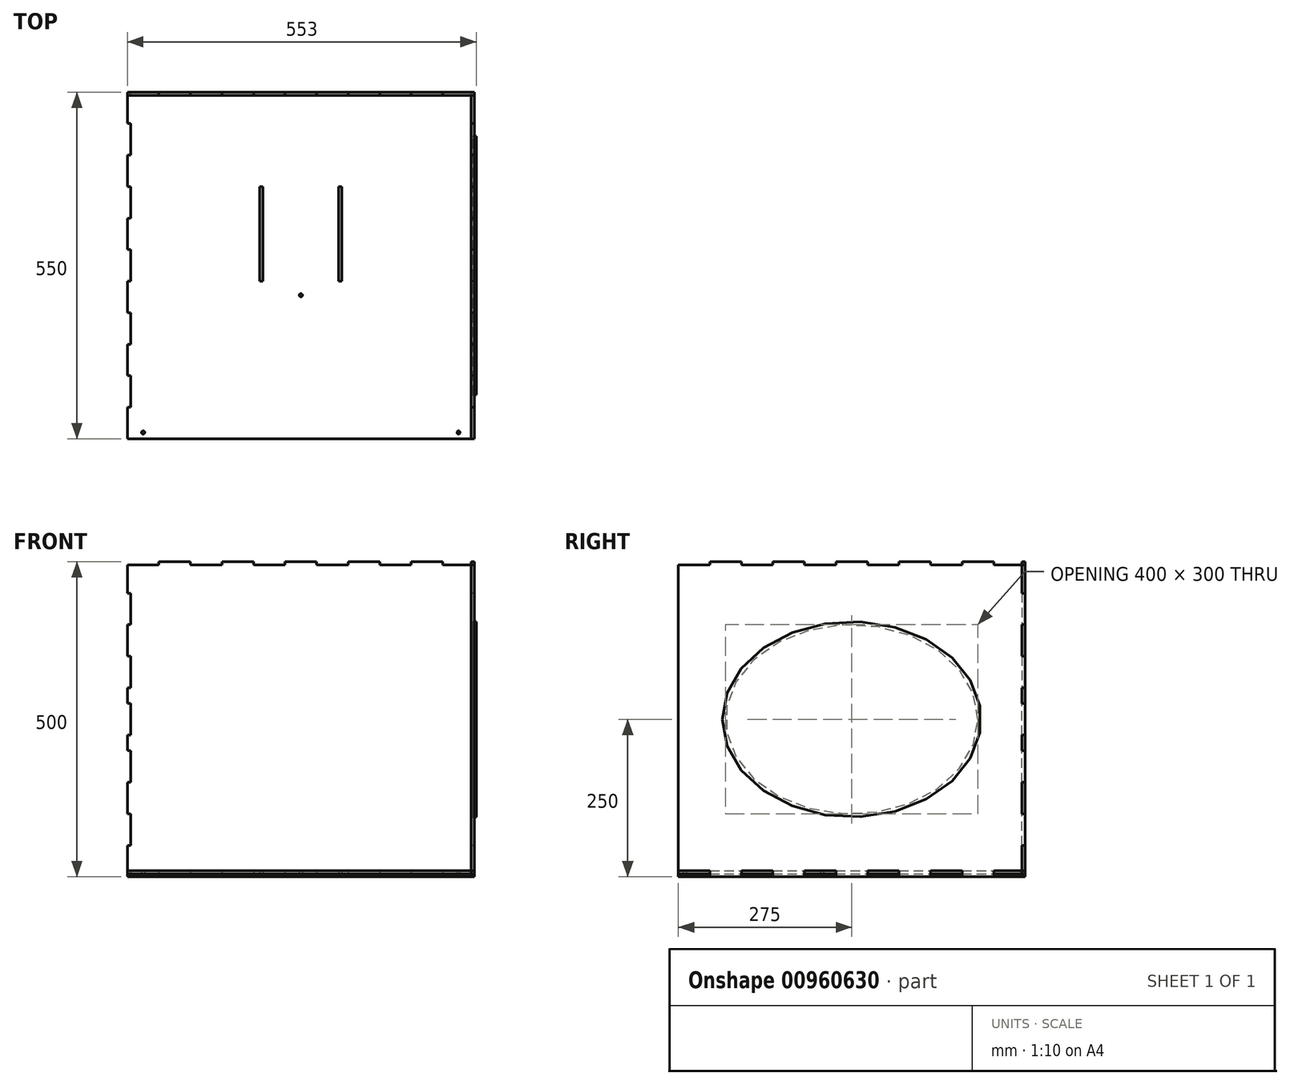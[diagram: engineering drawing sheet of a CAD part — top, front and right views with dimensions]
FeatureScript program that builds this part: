
annotation { "Feature Type Name" : "Feature", "Feature Type Description" : "" }
export const myFeature = defineFeature(function(context is Context, id is Id, definition is map)
    precondition{}
    {
        {
            var Q0;
            Q0=qCreatedBy(makeId("Top.planeOp"),FACE);
            var sketch = newSketch(context, id + "F0", { "sketchPlane" : qUnion([Q0])});
            skPoint(sketch, "E0.middle", {"position": v(0, 0) * mm});
            skLineSegment(sketch, "E1", {"start": v(275, -275) * mm, "end": v(275, -225) * mm});
            skLineSegment(sketch, "E2", {"start": v(275, -225) * mm, "end": v(270, -225) * mm});
            skLineSegment(sketch, "E3", {"start": v(270, -225) * mm, "end": v(270, -175) * mm});
            skLineSegment(sketch, "E4", {"start": v(270, -175) * mm, "end": v(275, -175) * mm});
            skLineSegment(sketch, "E5.0.1.0", {"start": v(270, -125) * mm, "end": v(270, -75) * mm});
            skLineSegment(sketch, "E5.0.1.1", {"start": v(270, -75) * mm, "end": v(275, -75) * mm});
            skLineSegment(sketch, "E5.0.1.2", {"start": v(275, -175) * mm, "end": v(275, -125) * mm});
            skLineSegment(sketch, "E5.0.1.3", {"start": v(275, -125) * mm, "end": v(270, -125) * mm});
            skLineSegment(sketch, "E5.0.2.0", {"start": v(270, -25) * mm, "end": v(270, 25) * mm});
            skLineSegment(sketch, "E5.0.2.1", {"start": v(270, 25) * mm, "end": v(275, 25) * mm});
            skLineSegment(sketch, "E5.0.2.2", {"start": v(275, -75) * mm, "end": v(275, -25) * mm});
            skLineSegment(sketch, "E5.0.2.3", {"start": v(275, -25) * mm, "end": v(270, -25) * mm});
            skLineSegment(sketch, "E5.0.3.0", {"start": v(270, 75) * mm, "end": v(270, 125) * mm});
            skLineSegment(sketch, "E5.0.3.1", {"start": v(270, 125) * mm, "end": v(275, 125) * mm});
            skLineSegment(sketch, "E5.0.3.2", {"start": v(275, 25) * mm, "end": v(275, 75) * mm});
            skLineSegment(sketch, "E5.0.3.3", {"start": v(275, 75) * mm, "end": v(270, 75) * mm});
            skLineSegment(sketch, "E5.0.4.0", {"start": v(270, 175) * mm, "end": v(270, 225) * mm});
            skLineSegment(sketch, "E5.0.4.1", {"start": v(270, 225) * mm, "end": v(275, 225) * mm});
            skLineSegment(sketch, "E5.0.4.2", {"start": v(275, 125) * mm, "end": v(275, 175) * mm});
            skLineSegment(sketch, "E5.0.4.3", {"start": v(275, 175) * mm, "end": v(270, 175) * mm});
            skLineSegment(sketch, "E5.direction1", {"start": v(275, -275) * mm, "end": v(300, -275) * mm, "construction": true});
            skLineSegment(sketch, "E5.direction2", {"start": v(275, -275) * mm, "end": v(275, -175) * mm, "construction": true});
            skLineSegment(sketch, "E6", {"start": v(-275, -275) * mm, "end": v(-275, -225) * mm});
            skLineSegment(sketch, "E7", {"start": v(-275, -225) * mm, "end": v(-270, -225) * mm});
            skLineSegment(sketch, "E8", {"start": v(-270, -225) * mm, "end": v(-270, -175) * mm});
            skLineSegment(sketch, "E9", {"start": v(-270, -175) * mm, "end": v(-275, -175) * mm});
            skLineSegment(sketch, "E10.0.1.0", {"start": v(-270, -125) * mm, "end": v(-270, -75) * mm});
            skLineSegment(sketch, "E10.0.1.1", {"start": v(-275, -175) * mm, "end": v(-275, -125) * mm});
            skLineSegment(sketch, "E10.0.1.2", {"start": v(-270, -75) * mm, "end": v(-275, -75) * mm});
            skLineSegment(sketch, "E10.0.1.3", {"start": v(-275, -125) * mm, "end": v(-270, -125) * mm});
            skLineSegment(sketch, "E10.0.2.0", {"start": v(-270, -25) * mm, "end": v(-270, 25) * mm});
            skLineSegment(sketch, "E10.0.2.1", {"start": v(-275, -75) * mm, "end": v(-275, -25) * mm});
            skLineSegment(sketch, "E10.0.2.2", {"start": v(-270, 25) * mm, "end": v(-275, 25) * mm});
            skLineSegment(sketch, "E10.0.2.3", {"start": v(-275, -25) * mm, "end": v(-270, -25) * mm});
            skLineSegment(sketch, "E10.0.3.0", {"start": v(-270, 75) * mm, "end": v(-270, 125) * mm});
            skLineSegment(sketch, "E10.0.3.1", {"start": v(-275, 25) * mm, "end": v(-275, 75) * mm});
            skLineSegment(sketch, "E10.0.3.2", {"start": v(-270, 125) * mm, "end": v(-275, 125) * mm});
            skLineSegment(sketch, "E10.0.3.3", {"start": v(-275, 75) * mm, "end": v(-270, 75) * mm});
            skLineSegment(sketch, "E10.0.4.0", {"start": v(-270, 175) * mm, "end": v(-270, 225) * mm});
            skLineSegment(sketch, "E10.0.4.1", {"start": v(-275, 125) * mm, "end": v(-275, 175) * mm});
            skLineSegment(sketch, "E10.0.4.2", {"start": v(-270, 225) * mm, "end": v(-275, 225) * mm});
            skLineSegment(sketch, "E10.0.4.3", {"start": v(-275, 175) * mm, "end": v(-270, 175) * mm});
            skLineSegment(sketch, "E10.direction1", {"start": v(-275, -275) * mm, "end": v(-250, -275) * mm, "construction": true});
            skLineSegment(sketch, "E10.direction2", {"start": v(-275, -275) * mm, "end": v(-275, -175) * mm, "construction": true});
            skLineSegment(sketch, "E11", {"start": v(-275, -275) * mm, "end": v(275, -275) * mm});
            skLineSegment(sketch, "E12", {"start": v(275, 225) * mm, "end": v(275, 275) * mm});
            skLineSegment(sketch, "E13", {"start": v(-275, 225) * mm, "end": v(-275, 275) * mm});
            skLineSegment(sketch, "E14", {"start": v(-275, 275) * mm, "end": v(-225, 275) * mm});
            skLineSegment(sketch, "E15", {"start": v(-225, 275) * mm, "end": v(-225, 270) * mm});
            skLineSegment(sketch, "E16", {"start": v(-225, 270) * mm, "end": v(-175, 270) * mm});
            skLineSegment(sketch, "E17", {"start": v(-175, 270) * mm, "end": v(-175, 275) * mm});
            skLineSegment(sketch, "E18.1.0.0", {"start": v(-175, 275) * mm, "end": v(-125, 275) * mm});
            skLineSegment(sketch, "E18.1.0.1", {"start": v(-125, 270) * mm, "end": v(-75, 270) * mm});
            skLineSegment(sketch, "E18.1.0.2", {"start": v(-75, 270) * mm, "end": v(-75, 275) * mm});
            skLineSegment(sketch, "E18.1.0.3", {"start": v(-125, 275) * mm, "end": v(-125, 270) * mm});
            skLineSegment(sketch, "E18.2.0.0", {"start": v(-75, 275) * mm, "end": v(-25, 275) * mm});
            skLineSegment(sketch, "E18.2.0.1", {"start": v(-25, 270) * mm, "end": v(25, 270) * mm});
            skLineSegment(sketch, "E18.2.0.2", {"start": v(25, 270) * mm, "end": v(25, 275) * mm});
            skLineSegment(sketch, "E18.2.0.3", {"start": v(-25, 275) * mm, "end": v(-25, 270) * mm});
            skLineSegment(sketch, "E18.3.0.0", {"start": v(25, 275) * mm, "end": v(75, 275) * mm});
            skLineSegment(sketch, "E18.3.0.1", {"start": v(75, 270) * mm, "end": v(125, 270) * mm});
            skLineSegment(sketch, "E18.3.0.2", {"start": v(125, 270) * mm, "end": v(125, 275) * mm});
            skLineSegment(sketch, "E18.3.0.3", {"start": v(75, 275) * mm, "end": v(75, 270) * mm});
            skLineSegment(sketch, "E18.4.0.0", {"start": v(125, 275) * mm, "end": v(175, 275) * mm});
            skLineSegment(sketch, "E18.4.0.1", {"start": v(175, 270) * mm, "end": v(225, 270) * mm});
            skLineSegment(sketch, "E18.4.0.2", {"start": v(225, 270) * mm, "end": v(225, 275) * mm});
            skLineSegment(sketch, "E18.4.0.3", {"start": v(175, 275) * mm, "end": v(175, 270) * mm});
            skLineSegment(sketch, "E19", {"start": v(225, 275) * mm, "end": v(275, 275) * mm});
            skCircle(sketch, "E20", {"center": v(0, -47.26) * mm, "radius": 2.5 * mm});
            skLineSegment(sketch, "E21.bottom", {"start": v(-65, 125) * mm, "end": v(-60, 125) * mm});
            skLineSegment(sketch, "E21.top", {"start": v(-65, -25) * mm, "end": v(-60, -25) * mm});
            skLineSegment(sketch, "E21.left", {"start": v(-65, 125) * mm, "end": v(-65, -25) * mm});
            skLineSegment(sketch, "E21.right", {"start": v(-60, 125) * mm, "end": v(-60, -25) * mm});
            skLineSegment(sketch, "E22", {"start": v(0, 0) * mm, "end": v(0, -94.7) * mm, "construction": true});
            skLineSegment(sketch, "E23.MirrorCS", {"start": v(65, -25) * mm, "end": v(60, -25) * mm});
            skLineSegment(sketch, "E24.MirrorCS", {"start": v(65, 125) * mm, "end": v(60, 125) * mm});
            skLineSegment(sketch, "E25.MirrorCS", {"start": v(60, 125) * mm, "end": v(60, -25) * mm});
            skLineSegment(sketch, "E26.MirrorCS", {"start": v(65, 125) * mm, "end": v(65, -25) * mm});
            skCircle(sketch, "E27", {"center": v(250, -265) * mm, "radius": 2.5 * mm});
            skCircle(sketch, "E28", {"center": v(-250, -265) * mm, "radius": 2.5 * mm});
            skSolve(sketch);
        }
        {
            var Q0;
            Q0=makeQuery(id+"F0.imprint","IMPRINT",FACE,{"disambiguationData":[TD([[makeQuery(id+"F0.imprint","IMPRINT",EDGE,{"derivedFrom":sQuery(id+"F0.wireOp",EDGE,"E1")}),1.0]])]});
            var Q1;
            Q1=makeQuery(id+"F0.imprint","IMPRINT",FACE,{"disambiguationData":[TD([[makeQuery(id+"F0.imprint","IMPRINT",EDGE,{"derivedFrom":sQuery(id+"F0.wireOp",EDGE,"E20")}),1.0]])]});
            var Q2;
            Q2=makeQuery(id+"F0.imprint","IMPRINT",FACE,{"disambiguationData":[TD([[makeQuery(id+"F0.imprint","IMPRINT",EDGE,{"derivedFrom":sQuery(id+"F0.wireOp",EDGE,"E21.bottom")}),-1.0]])]});
            var Q3;
            Q3=makeQuery(id+"F0.imprint","IMPRINT",FACE,{"disambiguationData":[TD([[makeQuery(id+"F0.imprint","IMPRINT",EDGE,{"derivedFrom":sQuery(id+"F0.wireOp",EDGE,"E23.MirrorCS")}),-1.0]])]});
            extrude(context, id + "F1", {"entities" : qUnion([Q0, Q1, Q2, Q3]), "oppositeDirection" : true, "depth" : 5 * mm, "offsetDistance" : 25 * mm});
        }
        {
            var Q0;
            Q0=makeQuery(id+"F1.opExtrude","SWEPT_FACE",FACE,{"disambiguationData":[OSD([sQuery(id+"F0.wireOp",EDGE,"E1")])]});
            var sketch = newSketch(context, id + "F2", { "sketchPlane" : qUnion([Q0])});
            skLineSegment(sketch, "E29.top", {"start": v(-275, 545) * mm, "end": v(275, 545) * mm, "construction": true});
            skLineSegment(sketch, "E29.left", {"start": v(-275, -5) * mm, "end": v(-275, 545) * mm, "construction": true});
            skLineSegment(sketch, "E30", {"start": v(-275, 0) * mm, "end": v(-225, 0) * mm});
            skLineSegment(sketch, "E31", {"start": v(-225, 0) * mm, "end": v(-225, -5) * mm});
            skLineSegment(sketch, "E32", {"start": v(-225, -5) * mm, "end": v(-175, -5) * mm});
            skLineSegment(sketch, "E33", {"start": v(-175, -5) * mm, "end": v(-175, 0) * mm});
            skLineSegment(sketch, "E34.1.0.0", {"start": v(-175, 0) * mm, "end": v(-125, 0) * mm});
            skLineSegment(sketch, "E34.1.0.1", {"start": v(-125, 0) * mm, "end": v(-125, -5) * mm});
            skLineSegment(sketch, "E34.1.0.2", {"start": v(-125, -5) * mm, "end": v(-75, -5) * mm});
            skLineSegment(sketch, "E34.1.0.3", {"start": v(-75, -5) * mm, "end": v(-75, 0) * mm});
            skLineSegment(sketch, "E34.2.0.0", {"start": v(-75, 0) * mm, "end": v(-25, 0) * mm});
            skLineSegment(sketch, "E34.2.0.1", {"start": v(-25, 0) * mm, "end": v(-25, -5) * mm});
            skLineSegment(sketch, "E34.2.0.2", {"start": v(-25, -5) * mm, "end": v(25, -5) * mm});
            skLineSegment(sketch, "E34.2.0.3", {"start": v(25, -5) * mm, "end": v(25, 0) * mm});
            skLineSegment(sketch, "E34.3.0.0", {"start": v(25, 0) * mm, "end": v(75, 0) * mm});
            skLineSegment(sketch, "E34.3.0.1", {"start": v(75, 0) * mm, "end": v(75, -5) * mm});
            skLineSegment(sketch, "E34.3.0.2", {"start": v(75, -5) * mm, "end": v(125, -5) * mm});
            skLineSegment(sketch, "E34.3.0.3", {"start": v(125, -5) * mm, "end": v(125, 0) * mm});
            skLineSegment(sketch, "E34.4.0.0", {"start": v(125, 0) * mm, "end": v(175, 0) * mm});
            skLineSegment(sketch, "E34.4.0.1", {"start": v(175, 0) * mm, "end": v(175, -5) * mm});
            skLineSegment(sketch, "E34.4.0.2", {"start": v(175, -5) * mm, "end": v(225, -5) * mm});
            skLineSegment(sketch, "E34.4.0.3", {"start": v(225, -5) * mm, "end": v(225, 0) * mm});
            skLineSegment(sketch, "E34.direction1", {"start": v(-275, 0) * mm, "end": v(-175, 0) * mm, "construction": true});
            skLineSegment(sketch, "E35.direction1", {"start": v(275, -34.7) * mm, "end": v(300, -34.7) * mm, "construction": true});
            skLineSegment(sketch, "E36", {"start": v(225, 0) * mm, "end": v(270, 0) * mm});
            skLineSegment(sketch, "E37", {"start": v(270, 0) * mm, "end": v(270, 45) * mm});
            skLineSegment(sketch, "E38", {"start": v(270, 45) * mm, "end": v(275, 45) * mm});
            skLineSegment(sketch, "E39", {"start": v(275, 45) * mm, "end": v(275, 95) * mm});
            skLineSegment(sketch, "E40", {"start": v(275, 95) * mm, "end": v(270, 95) * mm});
            skLineSegment(sketch, "E41", {"start": v(270, 95) * mm, "end": v(270, 145) * mm});
            skLineSegment(sketch, "E42", {"start": v(275, 145) * mm, "end": v(270, 145) * mm});
            skLineSegment(sketch, "E43", {"start": v(-275, 245) * mm, "end": v(275, 245) * mm, "construction": true});
            skLineSegment(sketch, "E44", {"start": v(275, 145) * mm, "end": v(275, 195) * mm});
            skLineSegment(sketch, "E45", {"start": v(275, 195) * mm, "end": v(270, 195) * mm});
            skLineSegment(sketch, "E46", {"start": v(270, 195) * mm, "end": v(270, 220) * mm});
            skLineSegment(sketch, "E47", {"start": v(270, 220) * mm, "end": v(275, 220) * mm});
            skLineSegment(sketch, "E48", {"start": v(275, 220) * mm, "end": v(275, 245) * mm});
            skLineSegment(sketch, "E49", {"start": v(-275, 245) * mm, "end": v(-275, 0) * mm});
            skLineSegment(sketch, "E50.MirrorCS", {"start": v(-175, 495) * mm, "end": v(-175, 490) * mm});
            skLineSegment(sketch, "E51.MirrorCS", {"start": v(270, 445) * mm, "end": v(275, 445) * mm});
            skLineSegment(sketch, "E52.MirrorCS", {"start": v(275, 345) * mm, "end": v(270, 345) * mm});
            skLineSegment(sketch, "E53.MirrorCS", {"start": v(270, 270) * mm, "end": v(275, 270) * mm});
            skLineSegment(sketch, "E54.MirrorCS", {"start": v(275, 395) * mm, "end": v(270, 395) * mm});
            skLineSegment(sketch, "E55.MirrorCS", {"start": v(225, 495) * mm, "end": v(225, 490) * mm});
            skLineSegment(sketch, "E56.MirrorCS", {"start": v(75, 490) * mm, "end": v(75, 495) * mm});
            skLineSegment(sketch, "E57.MirrorCS", {"start": v(175, 490) * mm, "end": v(175, 495) * mm});
            skLineSegment(sketch, "E58.MirrorCS", {"start": v(125, 495) * mm, "end": v(125, 490) * mm});
            skLineSegment(sketch, "E59.MirrorCS", {"start": v(-125, 490) * mm, "end": v(-125, 495) * mm});
            skLineSegment(sketch, "E60.MirrorCS", {"start": v(275, 295) * mm, "end": v(270, 295) * mm});
            skLineSegment(sketch, "E61.MirrorCS", {"start": v(-75, 495) * mm, "end": v(-75, 490) * mm});
            skLineSegment(sketch, "E62.MirrorCS", {"start": v(-25, 490) * mm, "end": v(-25, 495) * mm});
            skLineSegment(sketch, "E63.MirrorCS", {"start": v(25, 495) * mm, "end": v(25, 490) * mm});
            skLineSegment(sketch, "E64.MirrorCS", {"start": v(275, 270) * mm, "end": v(275, 245) * mm});
            skLineSegment(sketch, "E65.MirrorCS", {"start": v(-225, 490) * mm, "end": v(-225, 495) * mm});
            skLineSegment(sketch, "E66.MirrorCS", {"start": v(270, 295) * mm, "end": v(270, 270) * mm});
            skLineSegment(sketch, "E67.MirrorCS", {"start": v(225, 490) * mm, "end": v(270, 490) * mm});
            skLineSegment(sketch, "E68.MirrorCS", {"start": v(-275, 490) * mm, "end": v(-225, 490) * mm});
            skLineSegment(sketch, "E69.MirrorCS", {"start": v(275, 445) * mm, "end": v(275, 395) * mm});
            skLineSegment(sketch, "E70.MirrorCS", {"start": v(270, 490) * mm, "end": v(270, 445) * mm});
            skLineSegment(sketch, "E71.MirrorCS", {"start": v(275, 345) * mm, "end": v(275, 295) * mm});
            skLineSegment(sketch, "E72.MirrorCS", {"start": v(125, 490) * mm, "end": v(175, 490) * mm});
            skLineSegment(sketch, "E73.MirrorCS", {"start": v(-175, 490) * mm, "end": v(-125, 490) * mm});
            skLineSegment(sketch, "E74.MirrorCS", {"start": v(175, 495) * mm, "end": v(225, 495) * mm});
            skLineSegment(sketch, "E75.MirrorCS", {"start": v(270, 395) * mm, "end": v(270, 345) * mm});
            skLineSegment(sketch, "E76.MirrorCS", {"start": v(-225, 495) * mm, "end": v(-175, 495) * mm});
            skLineSegment(sketch, "E77.MirrorCS", {"start": v(-75, 490) * mm, "end": v(-25, 490) * mm});
            skLineSegment(sketch, "E78.MirrorCS", {"start": v(75, 495) * mm, "end": v(125, 495) * mm});
            skLineSegment(sketch, "E79.MirrorCS", {"start": v(25, 490) * mm, "end": v(75, 490) * mm});
            skLineSegment(sketch, "E80.MirrorCS", {"start": v(-25, 495) * mm, "end": v(25, 495) * mm});
            skLineSegment(sketch, "E81.MirrorCS", {"start": v(-275, 245) * mm, "end": v(-275, 490) * mm});
            skLineSegment(sketch, "E82.MirrorCS", {"start": v(-125, 495) * mm, "end": v(-75, 495) * mm});
            skLineSegment(sketch, "E83", {"start": v(0, 619.16) * mm, "end": v(0, -145.27) * mm, "construction": true});
            skEllipse(sketch, "E84", {"center": v(0, 245) * mm, "majorRadius": 200 * mm, "minorRadius": 150 * mm, "majorAxis": v(1, 0)});
            skEllipse(sketch, "E85", {"center": v(0, 245) * mm, "majorRadius": 205 * mm, "minorRadius": 155 * mm, "majorAxis": v(-1, 0)});
            skSolve(sketch);
        }
        {
            var Q0;
            Q0=makeQuery(id+"F2.imprint","IMPRINT",FACE,{"disambiguationData":[TD([[makeQuery(id+"F2.imprint","IMPRINT",EDGE,{"derivedFrom":sQuery(id+"F2.wireOp",EDGE,"E30")}),1.0]])]});
            var Q1;
            Q1=makeQuery(id+"F2.imprint","IMPRINT",FACE,{"disambiguationData":[TD([[makeQuery(id+"F2.imprint","IMPRINT",EDGE,{"derivedFrom":sQuery(id+"F2.wireOp",EDGE,"E84")}),-1.0]])]});
            extrude(context, id + "F3", {"entities" : qUnion([Q0, Q1]), "oppositeDirection" : true, "depth" : 5 * mm, "offsetDistance" : 25 * mm});
        }
        {
            var Q0;
            Q0=makeQuery(id+"F1.opExtrude","SWEPT_FACE",FACE,{"disambiguationData":[OSD([sQuery(id+"F0.wireOp",EDGE,"E19")])]});
            var sketch = newSketch(context, id + "F4", { "sketchPlane" : qUnion([Q0])});
            skLineSegment(sketch, "E86.top", {"start": v(-275, 545) * mm, "end": v(275, 545) * mm, "construction": true});
            skLineSegment(sketch, "E87", {"start": v(-225, -5) * mm, "end": v(-175, -5) * mm});
            skLineSegment(sketch, "E88", {"start": v(-175, -5) * mm, "end": v(-175, 0) * mm});
            skLineSegment(sketch, "E89", {"start": v(-225, -5) * mm, "end": v(-225, 0) * mm});
            skLineSegment(sketch, "E90", {"start": v(-225, 0) * mm, "end": v(-275, 0) * mm});
            skLineSegment(sketch, "E91.1.0.0", {"start": v(-125, 0) * mm, "end": v(-175, 0) * mm});
            skLineSegment(sketch, "E91.1.0.1", {"start": v(-125, -5) * mm, "end": v(-125, 0) * mm});
            skLineSegment(sketch, "E91.1.0.2", {"start": v(-125, -5) * mm, "end": v(-75, -5) * mm});
            skLineSegment(sketch, "E91.1.0.3", {"start": v(-75, -5) * mm, "end": v(-75, 0) * mm});
            skLineSegment(sketch, "E91.2.0.0", {"start": v(-25, 0) * mm, "end": v(-75, 0) * mm});
            skLineSegment(sketch, "E91.2.0.1", {"start": v(-25, -5) * mm, "end": v(-25, 0) * mm});
            skLineSegment(sketch, "E91.2.0.2", {"start": v(-25, -5) * mm, "end": v(25, -5) * mm});
            skLineSegment(sketch, "E91.2.0.3", {"start": v(25, -5) * mm, "end": v(25, 0) * mm});
            skLineSegment(sketch, "E91.3.0.0", {"start": v(75, 0) * mm, "end": v(25, 0) * mm});
            skLineSegment(sketch, "E91.3.0.1", {"start": v(75, -5) * mm, "end": v(75, 0) * mm});
            skLineSegment(sketch, "E91.3.0.2", {"start": v(75, -5) * mm, "end": v(125, -5) * mm});
            skLineSegment(sketch, "E91.3.0.3", {"start": v(125, -5) * mm, "end": v(125, 0) * mm});
            skLineSegment(sketch, "E91.4.0.0", {"start": v(175, 0) * mm, "end": v(125, 0) * mm});
            skLineSegment(sketch, "E91.4.0.1", {"start": v(175, -5) * mm, "end": v(175, 0) * mm});
            skLineSegment(sketch, "E91.4.0.2", {"start": v(175, -5) * mm, "end": v(225, -5) * mm});
            skLineSegment(sketch, "E91.4.0.3", {"start": v(225, -5) * mm, "end": v(225, 0) * mm});
            skLineSegment(sketch, "E92", {"start": v(225, 0) * mm, "end": v(275, 0) * mm});
            skLineSegment(sketch, "E93", {"start": v(-275, 0) * mm, "end": v(-275, 45) * mm});
            skLineSegment(sketch, "E94", {"start": v(-275, 45) * mm, "end": v(-270, 45) * mm});
            skLineSegment(sketch, "E95", {"start": v(-270, 45) * mm, "end": v(-270, 95) * mm});
            skLineSegment(sketch, "E96", {"start": v(-270, 95) * mm, "end": v(-275, 95) * mm});
            skLineSegment(sketch, "E97", {"start": v(-275, 245) * mm, "end": v(275, 245) * mm, "construction": true});
            skLineSegment(sketch, "E98", {"start": v(0, 545) * mm, "end": v(0, -17.12) * mm, "construction": true});
            skLineSegment(sketch, "E99", {"start": v(-275, 95) * mm, "end": v(-275, 145) * mm});
            skLineSegment(sketch, "E100", {"start": v(-275, 145) * mm, "end": v(-270, 145) * mm});
            skLineSegment(sketch, "E101", {"start": v(-270, 145) * mm, "end": v(-270, 195) * mm});
            skLineSegment(sketch, "E102", {"start": v(-270, 195) * mm, "end": v(-275, 195) * mm});
            skLineSegment(sketch, "E103", {"start": v(-275, 195) * mm, "end": v(-275, 220) * mm});
            skLineSegment(sketch, "E104", {"start": v(-275, 220) * mm, "end": v(-270, 220) * mm});
            skLineSegment(sketch, "E105", {"start": v(-270, 220) * mm, "end": v(-270, 245) * mm});
            skLineSegment(sketch, "E106.MirrorCS", {"start": v(275, 0) * mm, "end": v(275, 45) * mm});
            skLineSegment(sketch, "E107.MirrorCS", {"start": v(275, 45) * mm, "end": v(270, 45) * mm});
            skLineSegment(sketch, "E108.MirrorCS", {"start": v(275, 145) * mm, "end": v(270, 145) * mm});
            skLineSegment(sketch, "E109.MirrorCS", {"start": v(270, 195) * mm, "end": v(275, 195) * mm});
            skLineSegment(sketch, "E110.MirrorCS", {"start": v(270, 95) * mm, "end": v(275, 95) * mm});
            skLineSegment(sketch, "E111.MirrorCS", {"start": v(275, 220) * mm, "end": v(270, 220) * mm});
            skLineSegment(sketch, "E112.MirrorCS", {"start": v(275, 195) * mm, "end": v(275, 220) * mm});
            skLineSegment(sketch, "E113.MirrorCS", {"start": v(270, 145) * mm, "end": v(270, 195) * mm});
            skLineSegment(sketch, "E114.MirrorCS", {"start": v(270, 220) * mm, "end": v(270, 245) * mm});
            skLineSegment(sketch, "E115.MirrorCS", {"start": v(275, 95) * mm, "end": v(275, 145) * mm});
            skLineSegment(sketch, "E116.MirrorCS", {"start": v(270, 45) * mm, "end": v(270, 95) * mm});
            skLineSegment(sketch, "E117.MirrorCS", {"start": v(-270, 270) * mm, "end": v(-270, 245) * mm});
            skLineSegment(sketch, "E118.MirrorCS", {"start": v(270, 270) * mm, "end": v(270, 245) * mm});
            skLineSegment(sketch, "E119.MirrorCS", {"start": v(-275, 345) * mm, "end": v(-270, 345) * mm});
            skLineSegment(sketch, "E120.MirrorCS", {"start": v(-275, 270) * mm, "end": v(-270, 270) * mm});
            skLineSegment(sketch, "E121.MirrorCS", {"start": v(-270, 395) * mm, "end": v(-275, 395) * mm});
            skLineSegment(sketch, "E122.MirrorCS", {"start": v(-125, 495) * mm, "end": v(-125, 490) * mm});
            skLineSegment(sketch, "E123.MirrorCS", {"start": v(175, 495) * mm, "end": v(175, 490) * mm});
            skLineSegment(sketch, "E124.MirrorCS", {"start": v(270, 295) * mm, "end": v(275, 295) * mm});
            skLineSegment(sketch, "E125.MirrorCS", {"start": v(-75, 495) * mm, "end": v(-75, 490) * mm});
            skLineSegment(sketch, "E126.MirrorCS", {"start": v(25, 495) * mm, "end": v(25, 490) * mm});
            skLineSegment(sketch, "E127.MirrorCS", {"start": v(-225, 495) * mm, "end": v(-225, 490) * mm});
            skLineSegment(sketch, "E128.MirrorCS", {"start": v(-275, 445) * mm, "end": v(-270, 445) * mm});
            skLineSegment(sketch, "E129.MirrorCS", {"start": v(275, 445) * mm, "end": v(270, 445) * mm});
            skLineSegment(sketch, "E130.MirrorCS", {"start": v(125, 495) * mm, "end": v(125, 490) * mm});
            skLineSegment(sketch, "E131.MirrorCS", {"start": v(275, 270) * mm, "end": v(270, 270) * mm});
            skLineSegment(sketch, "E132.MirrorCS", {"start": v(-175, 495) * mm, "end": v(-175, 490) * mm});
            skLineSegment(sketch, "E133.MirrorCS", {"start": v(270, 395) * mm, "end": v(275, 395) * mm});
            skLineSegment(sketch, "E134.MirrorCS", {"start": v(275, 345) * mm, "end": v(270, 345) * mm});
            skLineSegment(sketch, "E135.MirrorCS", {"start": v(-25, 495) * mm, "end": v(-25, 490) * mm});
            skLineSegment(sketch, "E136.MirrorCS", {"start": v(75, 495) * mm, "end": v(75, 490) * mm});
            skLineSegment(sketch, "E137.MirrorCS", {"start": v(225, 495) * mm, "end": v(225, 490) * mm});
            skLineSegment(sketch, "E138.MirrorCS", {"start": v(-270, 295) * mm, "end": v(-275, 295) * mm});
            skLineSegment(sketch, "E139.MirrorCS", {"start": v(-225, 495) * mm, "end": v(-175, 495) * mm});
            skLineSegment(sketch, "E140.MirrorCS", {"start": v(75, 490) * mm, "end": v(25, 490) * mm});
            skLineSegment(sketch, "E141.MirrorCS", {"start": v(275, 295) * mm, "end": v(275, 270) * mm});
            skLineSegment(sketch, "E142.MirrorCS", {"start": v(-25, 490) * mm, "end": v(-75, 490) * mm});
            skLineSegment(sketch, "E143.MirrorCS", {"start": v(270, 445) * mm, "end": v(270, 395) * mm});
            skLineSegment(sketch, "E144.MirrorCS", {"start": v(225, 490) * mm, "end": v(275, 490) * mm});
            skLineSegment(sketch, "E145.MirrorCS", {"start": v(275, 490) * mm, "end": v(275, 445) * mm});
            skLineSegment(sketch, "E146.MirrorCS", {"start": v(-270, 445) * mm, "end": v(-270, 395) * mm});
            skLineSegment(sketch, "E147.MirrorCS", {"start": v(-125, 490) * mm, "end": v(-175, 490) * mm});
            skLineSegment(sketch, "E148.MirrorCS", {"start": v(-225, 490) * mm, "end": v(-275, 490) * mm});
            skLineSegment(sketch, "E149.MirrorCS", {"start": v(270, 345) * mm, "end": v(270, 295) * mm});
            skLineSegment(sketch, "E150.MirrorCS", {"start": v(175, 490) * mm, "end": v(125, 490) * mm});
            skLineSegment(sketch, "E151.MirrorCS", {"start": v(-275, 490) * mm, "end": v(-275, 445) * mm});
            skLineSegment(sketch, "E152.MirrorCS", {"start": v(-125, 495) * mm, "end": v(-75, 495) * mm});
            skLineSegment(sketch, "E153.MirrorCS", {"start": v(-270, 345) * mm, "end": v(-270, 295) * mm});
            skLineSegment(sketch, "E154.MirrorCS", {"start": v(175, 495) * mm, "end": v(225, 495) * mm});
            skLineSegment(sketch, "E155.MirrorCS", {"start": v(275, 395) * mm, "end": v(275, 345) * mm});
            skLineSegment(sketch, "E156.MirrorCS", {"start": v(75, 495) * mm, "end": v(125, 495) * mm});
            skLineSegment(sketch, "E157.MirrorCS", {"start": v(-25, 495) * mm, "end": v(25, 495) * mm});
            skLineSegment(sketch, "E158.MirrorCS", {"start": v(-275, 295) * mm, "end": v(-275, 270) * mm});
            skLineSegment(sketch, "E159.MirrorCS", {"start": v(-275, 395) * mm, "end": v(-275, 345) * mm});
            skSolve(sketch);
        }
        {
            var Q0;
            Q0=makeQuery(id+"F4.imprint","IMPRINT",FACE,{"disambiguationData":[TD([[makeQuery(id+"F4.imprint","IMPRINT",EDGE,{"derivedFrom":sQuery(id+"F4.wireOp",EDGE,"E87")}),1.0]])]});
            extrude(context, id + "F5", {"entities" : qUnion([Q0]), "oppositeDirection" : true, "depth" : 5 * mm, "offsetDistance" : 25 * mm});
        }
        {
            var Q0;
            Q0=makeQuery(id+"F0.imprint","IMPRINT",FACE,{"disambiguationData":[TD([[makeQuery(id+"F0.imprint","IMPRINT",EDGE,{"derivedFrom":sQuery(id+"F0.wireOp",EDGE,"E1")}),1.0]])]});
            extrude(context, id + "F6", {"entities" : qUnion([Q0]), "depth" : 5 * mm, "offsetDistance" : 25 * mm});
        }
        {
            var Q0;
            Q0=makeQuery(id+"F2.imprint","IMPRINT",FACE,{"disambiguationData":[TD([[makeQuery(id+"F2.imprint","IMPRINT",EDGE,{"derivedFrom":sQuery(id+"F2.wireOp",EDGE,"E84")}),-1.0]])]});
            var Q1;
            Q1=sQuery(id+"F2.wireOp",EDGE,"E85");
            extrude(context, id + "F7", {"entities" : qUnion([Q0]), "operationType" : NewBodyOperationType.REMOVE, "surfaceEntities" : qUnion([Q1]), "oppositeDirection" : true, "depth" : 3 * mm, "offsetDistance" : 25 * mm});
        }
        {
            var Q0;
            Q0=makeQuery(id+"F2.imprint","IMPRINT",FACE,{"disambiguationData":[TD([[makeQuery(id+"F2.imprint","IMPRINT",EDGE,{"derivedFrom":sQuery(id+"F2.wireOp",EDGE,"E84")}),-1.0]])]});
            var Q1;
            Q1=makeQuery(id+"F2.imprint","IMPRINT",FACE,{"disambiguationData":[TD([[makeQuery(id+"F2.imprint","IMPRINT",EDGE,{"derivedFrom":sQuery(id+"F2.wireOp",EDGE,"E84")}),1.0]])]});
            var Q2;
            Q2=sQuery(id+"F2.wireOp",EDGE,"E85");
            extrude(context, id + "F8", {"entities" : qUnion([Q0, Q1]), "surfaceEntities" : qUnion([Q2]), "depth" : 3 * mm, "offsetDistance" : 25 * mm});
        }
    });
